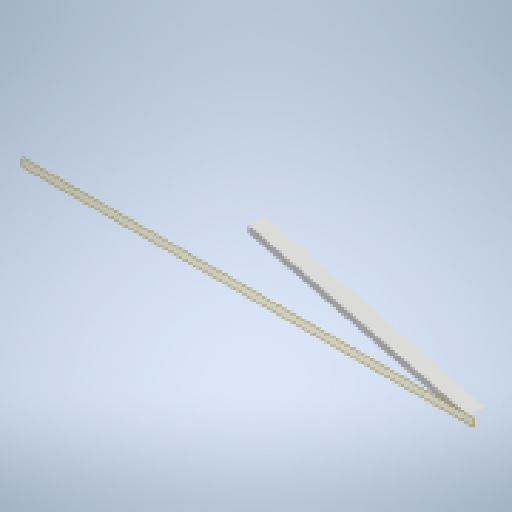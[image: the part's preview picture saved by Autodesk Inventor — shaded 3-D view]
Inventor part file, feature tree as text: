
AUTODESK INVENTOR PART (.ipt)
format: ipt  version: 2025 (Build 290162000, 162)  size: 141,824 bytes
history: native  units: in
note: dims shown in document units (in); Inventor stores cm internally (conversion verified against a paired STEP export)
features: other x5, reference x3, plane x1, extrude x1, sketch x1
ambient origin geometry x8: Origin, YZ Plane, XZ Plane, XY Plane, X Axis, Y Axis, Z Axis, Center Point
bodies: Solid1 (feature_tree)
feature tree (11):
  plane  "Work Plane1"
  extrude  "Extrusion1"  TaperAngle=90.0deg  [1 undecoded]
  sketch  "Sketch1"  dims[d0=12.0in d2=90.0deg d4=1.5in d5=3.5in d6=0.0in]
  reference  "Reference1"
  reference  "Reference2"
  reference  "Reference3"
  other  "<userpath>\Documents\USCTigerBurn24\Head.iam"
  other  "Head.iam"
  other  "2x4x96:4"
  other  "7'5''x2x4Correct:3"
  other  "2x4x96:3"
note: 1 required parameter value undecoded (feature->parameter linkage not recoverable at this tier; creation-order binding heuristic only, values carry confidence <= 0.55)
